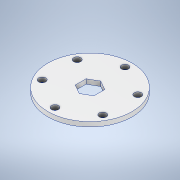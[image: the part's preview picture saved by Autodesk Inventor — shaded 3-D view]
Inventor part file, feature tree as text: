
AUTODESK INVENTOR PART (.ipt)
format: ipt  version: 2020 (Build 240168000, 168)  size: 152,064 bytes
history: native  units: in
note: dims shown in document units (in); Inventor stores cm internally (conversion verified against a paired STEP export)
features: sketch x3, extrude x2, hole x1, projected_geometry x1
ambient origin geometry x8: Origin, YZ Plane, XZ Plane, XY Plane, X Axis, Y Axis, Z Axis, Center Point
bodies: Solid1 (feature_tree)
feature tree (7):
  extrude  "Extrusion1"  Depth=0.5in
  hole  "Hole1"  [1 undecoded]
  extrude  "Extrusion2"  Depth=0.125in
  sketch  "Sketch1"  dims[d0=0.5in d2=2.25in]
  sketch  "Sketch2"  dims[d3=0.125in d4=0.0in d5=0.9375in]
  sketch  "Sketch3"  dims[d6=2.3622in d8=360.0deg d10=0.19in d11=0.75in d12=0.5in d13=0.2188in d14=0.5635in d15=1.0in d16=0.8108in d19=0.125in d20=1.25in d21=0.0in d22=0.0in]
  projected_geometry  "Projected Loop1"
note: 1 required parameter value undecoded (feature->parameter linkage not recoverable at this tier; creation-order binding heuristic only, values carry confidence <= 0.55)
